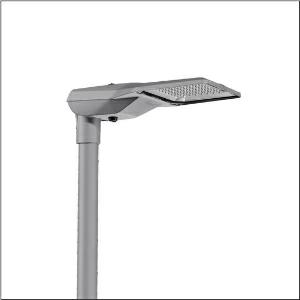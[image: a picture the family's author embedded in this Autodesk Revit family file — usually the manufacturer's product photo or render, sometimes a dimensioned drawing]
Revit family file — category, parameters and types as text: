
# Revit family: streetlight_sl_21_midi___pl52_5xe3h33t08mb_7712
name_source: partatom
category: Lighting Fixtures
units: mm (PartAtom-declared; Revit-internal decimal feet)

## family parameters
Cut with Voids When Loaded = No
Host = Face
Light Source = No
Part Type = Normal
Room Calculation Point = No
Round Connector Dimension = Use Diameter
Shared = No

## types (1)
- --- (1 x LED, 17960 lm, 136 W, 3000K)
    Apparent Load = 136 VA
    CIE Flux Codes = 27 59 98 100 100
    Color Rendering = 70
    Color Temperature = 3000K
    Default Elevation = 1800 mm
    Description = Streetlight SL 21 midi, mast luminaire, primary light control with lens, of PMMA, primary optical cover: cover, of toughened safety glass, transparent, light distribution: PL52, light emission: direct distribution, primary light characteristic: asymmetric, installation type: side-entry, post-top, LED, High Power LED, rated luminous flux: 17.960lm, luminous efficacy: 132lm/W, light colour: 730, colour temperature: 3000K, control: overheat protection, constant luminous flux control, time-dependent luminous flux control, flexible luminous flux parameterisation, presetting dimming logarithmic, mains connection: 230..240V, AC, 50/60Hz, start of lifetime: 136W, end of service life: 142W, reduction: 61W, luminaire housing, of diecast aluminium, powder-coated, Siteco® metallic grey (DB 702S), corrosivity category C5 mid according to DIN EN ISO 12944, please order mast flange separately, inclination adjustable: 0°, 5°, 10°, 15°, sealing non-destructively replaceable, multi-level sealing system, length: 644mm, width: 335mm, height: 110mm, mast flange for spigot size: 42mm (side-entry): 5XC10008XM4, 60/48mm (side-entry/post-top): 5XC10108XM2, 76/60mm (side-entry/post-top): 5XC10108XM1, Smart Interface below and above, protection rating (complete): IP66, insulation class (complete): insulation class II (safety insulation), certification: CE, ENEC, ENEC+, VDE, impact resistance: IK09, permissible operating ambient temperature for outdoor applications: -40..+50°C, standard-compliant lighting for roads and squares, packaging unit: 1 piece

Light Distribution: PL52
    Height = 111 mm
    Lamp = 1 x LED
    Lamp Light Flux = 17960 lm
    Lamp Power = 136 W
    Lamp count = 1
    Length = 644 mm
    Luminous efficacy = 132 lm/W
    Manufacturer = Siteco
    ModVariant = No
    Model = 5XE3H33T08MB
    Number of Poles = 1
    OnlyDefault = Yes
    Power Factor = 1
    Product Name = Streetlight SL 21 midi | PL52
    Product group = mast luminaire | pylon top
    ProductGroupID = 6100
    Protection Class = Protection class II
    Protection Degree = IP 66
    RLX_Detail_Level = 1
    RLX_Emergency_Light_Flux = 0 lm
    RLX_Emergency_Type = 0
    RLX_Emergency_Type_DB = No
    RlxData = <blob elided: 100121 chars, md5=a847ac9f>
    Socket = socket
    Standby Power = 0 W
    System Light Flux = 17960 lm
    System Power = 136 W
    Type Comments = factory setting: luminous flux: 100 % | dim-lin: 254 | 695 mA
    Type Image = l_1004304.jpg
    URL = http://relux.com
    VarID = @adj_124581
    Voltage = 0 V
    Weight = 0.00 kg
    Width = 336 mm

## geometry (parser evidence)
native form markers: Blend x4, Sweep x11
no freeform markers — native parametric forms only
